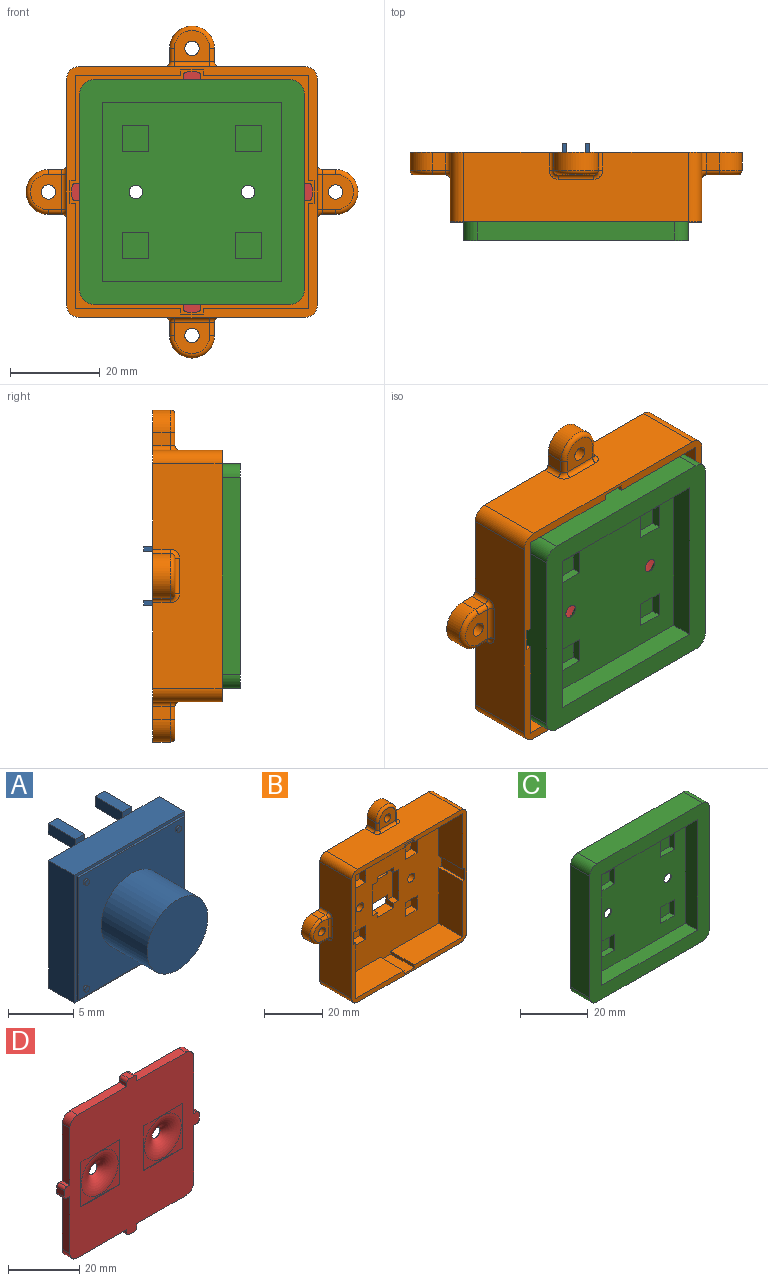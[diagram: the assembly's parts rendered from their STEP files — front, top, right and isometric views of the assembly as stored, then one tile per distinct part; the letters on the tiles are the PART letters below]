
ASSEMBLY  parts=4 mates=3
PART A: 45 faces, bbox 12x11x13 mm
  f0: plane 12x12mm, normal (0,1,0), area 142mm2, adj f17,f18,f19,f20,f22,f23,f24,f27
  f1: plane 11.5x11.5mm, normal (0,-1,0), area 97.3mm2, adj f2,f4,f6,f8,f10,f12,f13,f14
  f2: cylinder r=3.3mm len=6.6mm, axis (0,1,0), area 103.7mm2, adj f1,f3
  f3: plane 6.6x6.6mm, normal (0,-1,0), area 34.2mm2, adj f2
  f4: cylinder r=0.25mm len=0.5mm, axis (0,1,0), area 0.3mm2, adj f1,f5
  f5: plane 0.5x0.5mm, normal (0,-1,0), area 0.2mm2, adj f4
  f6: cylinder r=0.25mm len=0.5mm, axis (0,1,0), area 0.3mm2, adj f1,f7
  f7: plane 0.5x0.5mm, normal (0,-1,0), area 0.2mm2, adj f6
  f8: cylinder r=0.25mm len=0.5mm, axis (0,1,0), area 0.3mm2, adj f1,f9
  f9: plane 0.5x0.5mm, normal (0,-1,0), area 0.2mm2, adj f8
  f10: cylinder r=0.25mm len=0.5mm, axis (0,1,0), area 0.3mm2, adj f1,f11
  f11: plane 0.5x0.5mm, normal (0,-1,0), area 0.2mm2, adj f10
  f12: plane 11.5x0.2mm, normal (-1,0,0), area 2.3mm2, adj f1,f13,f15,f16
  f13: plane 11.5x0.2mm, normal (0,0,1), area 2.3mm2, adj f1,f12,f14,f16
  f14: plane 11.5x0.2mm, normal (1,0,0), area 2.3mm2, adj f1,f13,f15,f16
  f15: plane 11.5x0.2mm, normal (0,0,-1), area 2.3mm2, adj f1,f12,f14,f16
  f16: plane 12x12mm, normal (0,-1,0), area 11.8mm2, adj f12,f13,f14,f15,f17,f18,f19,f20
  f17: plane 12x2.8mm, normal (-1,0,0), area 33.6mm2, adj f0,f16,f18,f20
  f18: plane 12x2.8mm, normal (0,0,1), area 33.6mm2, adj f0,f16,f17,f19,f26,f32
  f19: plane 12x2.8mm, normal (1,0,0), area 33.6mm2, adj f0,f16,f18,f20
  f20: plane 12x2.8mm, normal (0,0,-1), area 33.6mm2, adj f0,f16,f17,f19,f33,f39
  f21: plane 3x1mm, normal (0,0,1), area 3mm2, adj f22,f24,f25,f26
  f22: plane 3x1mm, normal (1,0,0), area 3mm2, adj f0,f21,f23,f25,f26
  f23: plane 3x1mm, normal (0,0,-1), area 3mm2, adj f0,f22,f24,f25
  f24: plane 3x1mm, normal (-1,0,0), area 3mm2, adj f0,f21,f23,f25,f26
  f25: plane 1x1mm, normal (0,1,0), area 1mm2, adj f21,f22,f23,f24
  f26: plane 1x0.5mm, normal (0,-1,0), area 0.5mm2, adj f18,f21,f22,f24
  f27: plane 3x1mm, normal (0,0,-1), area 3mm2, adj f0,f28,f30,f31
  f28: plane 3x1mm, normal (-1,0,0), area 3mm2, adj f0,f27,f29,f31,f32
  f29: plane 3x1mm, normal (0,0,1), area 3mm2, adj f28,f30,f31,f32
  f30: plane 3x1mm, normal (1,0,0), area 3mm2, adj f0,f27,f29,f31,f32
  f31: plane 1x1mm, normal (0,1,0), area 1mm2, adj f27,f28,f29,f30
  f32: plane 1x0.5mm, normal (0,-1,0), area 0.5mm2, adj f18,f28,f29,f30
  f33: plane 1x0.5mm, normal (0,-1,0), area 0.5mm2, adj f20,f34,f35,f36
  f34: plane 3x1mm, normal (1,0,0), area 3mm2, adj f0,f33,f35,f37,f38
  f35: plane 3x1mm, normal (0,0,-1), area 3mm2, adj f33,f34,f36,f38
  f36: plane 3x1mm, normal (-1,0,0), area 3mm2, adj f0,f33,f35,f37,f38
  f37: plane 3x1mm, normal (0,0,1), area 3mm2, adj f0,f34,f36,f38
  f38: plane 1x1mm, normal (0,1,0), area 1mm2, adj f34,f35,f36,f37
  f39: plane 1x0.5mm, normal (0,-1,0), area 0.5mm2, adj f20,f40,f41,f42
  f40: plane 3x1mm, normal (1,0,0), area 3mm2, adj f0,f39,f41,f43,f44
  f41: plane 3x1mm, normal (0,0,-1), area 3mm2, adj f39,f40,f42,f44
  f42: plane 3x1mm, normal (-1,0,0), area 3mm2, adj f0,f39,f41,f43,f44
  f43: plane 3x1mm, normal (0,0,1), area 3mm2, adj f0,f40,f42,f44
  f44: plane 1x1mm, normal (0,1,0), area 1mm2, adj f40,f41,f42,f43
PART B: 120 faces, bbox 74.8x15.5x74.8 mm
  f0: plane 54.4x54.4mm, normal (0,-1,0), area 2374.3mm2, adj f3,f4,f5,f6,f10,f11,f15,f16
  f1: plane 50x15.5mm, normal (1,0,0), area 704.7mm2, adj f7,f12,f45,f46,f84,f86,f88,f90
  f2: plane 50x15.5mm, normal (0,0,1), area 704.7mm2, adj f7,f12,f46,f47,f76,f78,f80,f82
  f3: plane 23.5x11.5mm, normal (1,0,0), area 270.2mm2, adj f0,f7,f31,f34
  f4: plane 23.5x11.5mm, normal (0,0,-1), area 270.2mm2, adj f0,f7,f30,f43
  f5: plane 23.5x11.5mm, normal (-1,0,0), area 270.2mm2, adj f0,f6,f7,f39
  f6: plane 23.5x11.5mm, normal (0,0,1), area 270.2mm2, adj f0,f5,f7,f37
  f7: plane 56x56mm, normal (0,-1,0), area 400.3mm2, adj f1,f2,f3,f4,f5,f6,f13,f14
  f8: plane 8x1mm, normal (0,0,-1), area 8mm2, adj f12,f17,f19,f27
  f9: plane 8x1mm, normal (0,0,1), area 8mm2, adj f10,f11,f12,f27
  f10: plane 4x4mm, normal (-1,0,0), area 10mm2, adj f0,f9,f12,f20,f21,f27
  f11: plane 4x4mm, normal (1,0,0), area 10mm2, adj f0,f9,f12,f20,f22,f27
  f12: plane 74x74mm, normal (0,1,0), area 3332.7mm2, adj f1,f2,f8,f9,f10,f11,f13,f14
  f13: plane 50x15.5mm, normal (-1,0,0), area 704.7mm2, adj f7,f12,f44,f47,f92,f94,f96,f98
  f14: plane 50x15.5mm, normal (0,0,-1), area 704.7mm2, adj f7,f12,f44,f45,f68,f70,f72,f74
  f15: cylinder r=1.7mm len=4mm, axis (0,1,0), area 42.7mm2, adj f0,f12
  f16: cylinder r=1.7mm len=4mm, axis (0,1,0), area 42.7mm2, adj f0,f12
  f17: plane 4x4mm, normal (1,0,0), area 10mm2, adj f0,f8,f12,f18,f24,f27
  f18: plane 8x4mm, normal (0,0,1), area 32mm2, adj f0,f12,f17,f19
  f19: plane 4x4mm, normal (-1,0,0), area 10mm2, adj f0,f8,f12,f18,f25,f27
  f20: plane 8x4mm, normal (0,0,-1), area 32mm2, adj f0,f10,f11,f12
  f21: plane 3x2.5mm, normal (0,0,-1), area 7.5mm2, adj f0,f10,f26,f27
  f22: plane 3x2.5mm, normal (0,0,-1), area 7.5mm2, adj f0,f11,f23,f27
  f23: plane 13x3mm, normal (1,0,0), area 39mm2, adj f0,f22,f24,f27
  f24: plane 3x2.5mm, normal (0,0,1), area 7.5mm2, adj f0,f17,f23,f27
  f25: plane 3x2.5mm, normal (0,0,1), area 7.5mm2, adj f0,f19,f26,f27
  f26: plane 13x3mm, normal (-1,0,0), area 39mm2, adj f0,f21,f25,f27
  f27: plane 13x13mm, normal (0,-1,0), area 137mm2, adj f8,f9,f10,f11,f17,f19,f21,f22
  f28: plane 23.5x11.5mm, normal (1,0,0), area 270.2mm2, adj f0,f7,f29,f32
  f29: plane 23.5x11.5mm, normal (0,0,-1), area 270.2mm2, adj f0,f7,f28,f42
  f30: plane 23.5x11.5mm, normal (-1,0,0), area 270.2mm2, adj f0,f4,f7,f38
  f31: plane 23.5x11.5mm, normal (0,0,1), area 270.2mm2, adj f0,f3,f7,f35
  f32: plane 11.5x1.2mm, normal (0,0,-1), area 13.8mm2, adj f0,f7,f28,f33
  f33: plane 11.5x5mm, normal (1,0,0), area 57.5mm2, adj f0,f7,f32,f34
  f34: plane 11.5x1.2mm, normal (0,0,1), area 13.8mm2, adj f0,f3,f7,f33
  f35: plane 11.5x1.2mm, normal (1,0,0), area 13.8mm2, adj f0,f7,f31,f36
  f36: plane 11.5x5mm, normal (0,0,1), area 57.5mm2, adj f0,f7,f35,f37
  f37: plane 11.5x1.2mm, normal (-1,0,0), area 13.8mm2, adj f0,f6,f7,f36
  f38: plane 11.5x1.2mm, normal (0,0,-1), area 13.8mm2, adj f0,f7,f30,f40
  f39: plane 11.5x1.2mm, normal (0,0,1), area 13.8mm2, adj f0,f5,f7,f40
  f40: plane 11.5x5mm, normal (-1,0,0), area 57.5mm2, adj f0,f7,f38,f39
  f41: plane 11.5x5mm, normal (0,0,-1), area 57.5mm2, adj f0,f7,f42,f43
  f42: plane 11.5x1.2mm, normal (1,0,0), area 13.8mm2, adj f0,f7,f29,f41
  f43: plane 11.5x1.2mm, normal (-1,0,0), area 13.8mm2, adj f0,f4,f7,f41
  f44: cylinder r=3mm len=15.5mm, axis (0,1,0), area 73mm2, adj f7,f12,f13,f14
  f45: cylinder r=3mm len=15.5mm, axis (0,-1,0), area 73mm2, adj f1,f7,f12,f14
  f46: cylinder r=3mm len=15.5mm, axis (0,1,0), area 73mm2, adj f1,f2,f7,f12
  f47: cylinder r=3mm len=15.5mm, axis (0,-1,0), area 73mm2, adj f2,f7,f12,f13
  f48: cylinder r=5mm len=10mm, axis (0,1,0), area 62.8mm2, adj f12,f49,f51,f79
  f49: plane 4x3mm, normal (-1,0,0), area 12mm2, adj f12,f48,f76,f77
  f50: cylinder r=1.6mm len=5mm, axis (0,1,0), area 50.3mm2, adj f12,f52
  f51: plane 4x3mm, normal (1,0,0), area 12mm2, adj f12,f48,f81,f83
  f52: plane 8x7mm, normal (0,-1,0), area 41.1mm2, adj f50,f77,f79,f80,f81
  f53: plane 4x3mm, normal (-1,0,0), area 12mm2, adj f12,f54,f73,f75
  f54: cylinder r=5mm len=10mm, axis (0,1,0), area 62.8mm2, adj f12,f53,f55,f71
  f55: plane 4x3mm, normal (1,0,0), area 12mm2, adj f12,f54,f68,f69
  f56: cylinder r=1.6mm len=5mm, axis (0,1,0), area 50.3mm2, adj f12,f57
  f57: plane 8x7mm, normal (0,-1,0), area 41.1mm2, adj f56,f69,f71,f72,f73
  f58: plane 4x3mm, normal (0,0,1), area 12mm2, adj f12,f59,f97,f99
  f59: cylinder r=5mm len=10mm, axis (0,1,0), area 62.8mm2, adj f12,f58,f60,f95
  f60: plane 4x3mm, normal (0,0,-1), area 12mm2, adj f12,f59,f92,f93
  f61: cylinder r=1.6mm len=5mm, axis (0,1,0), area 50.3mm2, adj f12,f62
  f62: plane 8x7mm, normal (0,-1,0), area 41.1mm2, adj f61,f93,f95,f96,f97
  f63: cylinder r=5mm len=10mm, axis (0,1,0), area 62.8mm2, adj f12,f64,f66,f87
  f64: plane 4x3mm, normal (0,0,1), area 12mm2, adj f12,f63,f84,f85
  f65: cylinder r=1.6mm len=5mm, axis (0,1,0), area 50.3mm2, adj f12,f67
  f66: plane 4x3mm, normal (0,0,-1), area 12mm2, adj f12,f63,f89,f91
  f67: plane 8x7mm, normal (0,-1,0), area 41.1mm2, adj f65,f85,f87,f88,f89
  f68: cylinder r=1mm len=4mm, axis (0,-1,0), area 6.3mm2, adj f12,f14,f55,f70
  f69: cylinder r=1mm len=3mm, axis (0,0,-1), area 4.7mm2, adj f55,f57,f70,f71
  f70: torus R=2mm, axis (0,0,1), area 3.4mm2, adj f14,f68,f69,f72
  f71: torus R=4mm, axis (0,-1,0), area 22.9mm2, adj f54,f57,f69,f73
  f72: cylinder r=1mm len=8mm, axis (1,0,0), area 12.6mm2, adj f14,f57,f70,f74
  f73: cylinder r=1mm len=3mm, axis (0,0,1), area 4.7mm2, adj f53,f57,f71,f74
  f74: torus R=2mm, axis (0,0,1), area 3.4mm2, adj f14,f72,f73,f75
  f75: cylinder r=1mm len=4mm, axis (0,1,0), area 6.3mm2, adj f12,f14,f53,f74
  f76: cylinder r=1mm len=4mm, axis (0,1,0), area 6.3mm2, adj f2,f12,f49,f78
  f77: cylinder r=1mm len=3mm, axis (0,0,1), area 4.7mm2, adj f49,f52,f78,f79
  f78: torus R=2mm, axis (0,0,1), area 3.4mm2, adj f2,f76,f77,f80
  f79: torus R=4mm, axis (0,-1,0), area 22.9mm2, adj f48,f52,f77,f81
  f80: cylinder r=1mm len=8mm, axis (-1,0,0), area 12.6mm2, adj f2,f52,f78,f82
  f81: cylinder r=1mm len=3mm, axis (0,0,-1), area 4.7mm2, adj f51,f52,f79,f82
  f82: torus R=2mm, axis (0,0,1), area 3.4mm2, adj f2,f80,f81,f83
  f83: cylinder r=1mm len=4mm, axis (0,-1,0), area 6.3mm2, adj f2,f12,f51,f82
  f84: cylinder r=1mm len=4mm, axis (0,1,0), area 6.3mm2, adj f1,f12,f64,f86
  f85: cylinder r=1mm len=3mm, axis (1,0,0), area 4.7mm2, adj f64,f67,f86,f87
  f86: torus R=2mm, axis (1,0,0), area 3.4mm2, adj f1,f84,f85,f88
  f87: torus R=4mm, axis (0,-1,0), area 22.9mm2, adj f63,f67,f85,f89
  f88: cylinder r=1mm len=8mm, axis (0,0,1), area 12.6mm2, adj f1,f67,f86,f90
  f89: cylinder r=1mm len=3mm, axis (-1,0,0), area 4.7mm2, adj f66,f67,f87,f90
  f90: torus R=2mm, axis (1,0,0), area 3.4mm2, adj f1,f88,f89,f91
  f91: cylinder r=1mm len=4mm, axis (0,-1,0), area 6.3mm2, adj f1,f12,f66,f90
  f92: cylinder r=1mm len=4mm, axis (0,-1,0), area 6.3mm2, adj f12,f13,f60,f94
  f93: cylinder r=1mm len=3mm, axis (-1,0,0), area 4.7mm2, adj f60,f62,f94,f95
  f94: torus R=2mm, axis (1,0,0), area 3.4mm2, adj f13,f92,f93,f96
  f95: torus R=4mm, axis (0,-1,0), area 22.9mm2, adj f59,f62,f93,f97
  f96: cylinder r=1mm len=8mm, axis (0,0,-1), area 12.6mm2, adj f13,f62,f94,f98
  f97: cylinder r=1mm len=3mm, axis (1,0,0), area 4.7mm2, adj f58,f62,f95,f98
  f98: torus R=2mm, axis (1,0,0), area 3.4mm2, adj f13,f96,f97,f99
  f99: cylinder r=1mm len=4mm, axis (0,1,0), area 6.3mm2, adj f12,f13,f58,f98
  f100: plane 5.8x3mm, normal (0,0,1), area 17.4mm2, adj f0,f101,f103,f104
  f101: plane 5.8x3mm, normal (-1,0,0), area 17.4mm2, adj f0,f100,f102,f104
  f102: plane 5.8x3mm, normal (0,0,-1), area 17.4mm2, adj f0,f101,f103,f104
  f103: plane 5.8x3mm, normal (1,0,0), area 17.4mm2, adj f0,f100,f102,f104
  f104: plane 5.8x5.8mm, normal (0,-1,0), area 33.6mm2, adj f100,f101,f102,f103
  f105: plane 5.8x3mm, normal (0,0,1), area 17.4mm2, adj f0,f106,f108,f109
  f106: plane 5.8x3mm, normal (-1,0,0), area 17.4mm2, adj f0,f105,f107,f109
  f107: plane 5.8x3mm, normal (0,0,-1), area 17.4mm2, adj f0,f106,f108,f109
  f108: plane 5.8x3mm, normal (1,0,0), area 17.4mm2, adj f0,f105,f107,f109
  f109: plane 5.8x5.8mm, normal (0,-1,0), area 33.6mm2, adj f105,f106,f107,f108
  f110: plane 5.8x3mm, normal (0,0,1), area 17.4mm2, adj f0,f111,f113,f114
  f111: plane 5.8x3mm, normal (-1,0,0), area 17.4mm2, adj f0,f110,f112,f114
  f112: plane 5.8x3mm, normal (0,0,-1), area 17.4mm2, adj f0,f111,f113,f114
  f113: plane 5.8x3mm, normal (1,0,0), area 17.4mm2, adj f0,f110,f112,f114
  f114: plane 5.8x5.8mm, normal (0,-1,0), area 33.6mm2, adj f110,f111,f112,f113
  f115: plane 5.8x3mm, normal (0,0,1), area 17.4mm2, adj f0,f116,f118,f119
  f116: plane 5.8x3mm, normal (-1,0,0), area 17.4mm2, adj f0,f115,f117,f119
  f117: plane 5.8x3mm, normal (0,0,-1), area 17.4mm2, adj f0,f116,f118,f119
  f118: plane 5.8x3mm, normal (1,0,0), area 17.4mm2, adj f0,f115,f117,f119
  f119: plane 5.8x5.8mm, normal (0,-1,0), area 33.6mm2, adj f115,f116,f117,f118
PART C: 47 faces, bbox 50x15.1x50 mm
  f0: plane 40x40mm, normal (0,-1,0), area 1451.3mm2, adj f6,f7,f8,f9,f25,f26,f27,f28
  f1: plane 50x50mm, normal (0,1,0), area 2018mm2, adj f2,f3,f4,f5,f11,f12,f13,f14
  f2: plane 44x8mm, normal (0,0,1), area 352mm2, adj f1,f10,f21,f24
  f3: plane 44x8mm, normal (-1,0,0), area 352mm2, adj f1,f10,f21,f22
  f4: plane 44x8mm, normal (0,0,-1), area 352mm2, adj f1,f10,f22,f23
  f5: plane 44x8mm, normal (1,0,0), area 352mm2, adj f1,f10,f23,f24
  f6: plane 40x5mm, normal (1,0,0), area 200mm2, adj f0,f7,f9,f10
  f7: plane 40x5mm, normal (0,0,-1), area 200mm2, adj f0,f6,f8,f10
  f8: plane 40x5mm, normal (-1,0,0), area 200mm2, adj f0,f7,f9,f10
  f9: plane 40x5mm, normal (0,0,1), area 200mm2, adj f0,f6,f8,f10
  f10: plane 50x50mm, normal (0,-1,0), area 892.3mm2, adj f2,f3,f4,f5,f6,f7,f8,f9
  f11: plane 15.4x0.2mm, normal (0,0,-1), area 3.1mm2, adj f1,f12,f14,f15
  f12: plane 15.4x0.2mm, normal (-1,0,0), area 3.1mm2, adj f1,f11,f13,f15
  f13: plane 15.4x0.2mm, normal (0,0,1), area 3.1mm2, adj f1,f12,f14,f15
  f14: plane 15.4x0.2mm, normal (1,0,0), area 3.1mm2, adj f1,f11,f13,f15
  f15: plane 15.4x15.4mm, normal (0,1,0), area 67.7mm2, adj f11,f12,f13,f14,f45
  f16: plane 15.4x0.2mm, normal (0,0,-1), area 3.1mm2, adj f1,f17,f19,f20
  f17: plane 15.4x0.2mm, normal (-1,0,0), area 3.1mm2, adj f1,f16,f18,f20
  f18: plane 15.4x0.2mm, normal (0,0,1), area 3.1mm2, adj f1,f17,f19,f20
  f19: plane 15.4x0.2mm, normal (1,0,0), area 3.1mm2, adj f1,f16,f18,f20
  f20: plane 15.4x15.4mm, normal (0,1,0), area 67.7mm2, adj f16,f17,f18,f19,f46
  f21: cylinder r=3mm len=8mm, axis (0,-1,0), area 37.7mm2, adj f1,f2,f3,f10
  f22: cylinder r=3mm len=8mm, axis (0,1,0), area 37.7mm2, adj f1,f3,f4,f10
  f23: cylinder r=3mm len=8mm, axis (0,-1,0), area 37.7mm2, adj f1,f4,f5,f10
  f24: cylinder r=3mm len=8mm, axis (0,1,0), area 37.7mm2, adj f1,f2,f5,f10
  f25: plane 5.8x2mm, normal (0,0,1), area 11.6mm2, adj f0,f26,f28,f29
  f26: plane 5.8x2mm, normal (-1,0,0), area 11.6mm2, adj f0,f25,f27,f29
  f27: plane 5.8x2mm, normal (0,0,-1), area 11.6mm2, adj f0,f26,f28,f29
  f28: plane 5.8x2mm, normal (1,0,0), area 11.6mm2, adj f0,f25,f27,f29
  f29: plane 5.8x5.8mm, normal (0,-1,0), area 33.6mm2, adj f25,f26,f27,f28
  f30: plane 5.8x2mm, normal (0,0,1), area 11.6mm2, adj f0,f31,f33,f34
  f31: plane 5.8x2mm, normal (-1,0,0), area 11.6mm2, adj f0,f30,f32,f34
  f32: plane 5.8x2mm, normal (0,0,-1), area 11.6mm2, adj f0,f31,f33,f34
  f33: plane 5.8x2mm, normal (1,0,0), area 11.6mm2, adj f0,f30,f32,f34
  f34: plane 5.8x5.8mm, normal (0,-1,0), area 33.6mm2, adj f30,f31,f32,f33
  f35: plane 5.8x2mm, normal (0,0,1), area 11.6mm2, adj f0,f36,f38,f39
  f36: plane 5.8x2mm, normal (-1,0,0), area 11.6mm2, adj f0,f35,f37,f39
  f37: plane 5.8x2mm, normal (0,0,-1), area 11.6mm2, adj f0,f36,f38,f39
  f38: plane 5.8x2mm, normal (1,0,0), area 11.6mm2, adj f0,f35,f37,f39
  f39: plane 5.8x5.8mm, normal (0,-1,0), area 33.6mm2, adj f35,f36,f37,f38
  f40: plane 5.8x2mm, normal (0,0,1), area 11.6mm2, adj f0,f41,f43,f44
  f41: plane 5.8x2mm, normal (-1,0,0), area 11.6mm2, adj f0,f40,f42,f44
  f42: plane 5.8x2mm, normal (0,0,-1), area 11.6mm2, adj f0,f41,f43,f44
  f43: plane 5.8x2mm, normal (1,0,0), area 11.6mm2, adj f0,f40,f42,f44
  f44: plane 5.8x5.8mm, normal (0,-1,0), area 33.6mm2, adj f40,f41,f42,f43
  f45: torus R=7.34mm, axis (0,1,0), area 177.3mm2, adj f0,f15
  f46: torus R=7.34mm, axis (0,1,0), area 177.3mm2, adj f0,f20
PART D: 66 faces, bbox 53.5x7.2x53.5 mm
  f0: plane 53.5x53.5mm, normal (0,-1,0), area 1962.2mm2, adj f2,f3,f4,f5,f6,f7,f8,f9
  f1: plane 53.5x53.5mm, normal (0,1,0), area 2283.8mm2, adj f2,f3,f4,f5,f6,f7,f8,f9
  f2: plane 3x1.2mm, normal (-1,0,0), area 3.6mm2, adj f0,f1,f3,f59
  f3: plane 19.55x3mm, normal (0,0,1), area 58.6mm2, adj f0,f1,f2,f24
  f4: plane 19.55x3mm, normal (-1,0,0), area 58.6mm2, adj f0,f1,f5,f24
  f5: plane 3x1.2mm, normal (0,0,1), area 3.6mm2, adj f0,f1,f4,f60
  f6: plane 3x2mm, normal (-1,0,0), area 6mm2, adj f0,f1,f60,f61
  f7: plane 3x1.2mm, normal (0,0,-1), area 3.6mm2, adj f0,f1,f8,f61
  f8: plane 19.55x3mm, normal (-1,0,0), area 58.6mm2, adj f0,f1,f7,f25
  f9: plane 19.55x3mm, normal (0,0,-1), area 58.6mm2, adj f0,f1,f10,f25
  f10: plane 3x1.2mm, normal (-1,0,0), area 3.6mm2, adj f0,f1,f9,f62
  f11: plane 3x2mm, normal (0,0,-1), area 6mm2, adj f0,f1,f62,f63
  f12: plane 3x1.2mm, normal (1,0,0), area 3.6mm2, adj f0,f1,f13,f63
  f13: plane 19.55x3mm, normal (0,0,-1), area 58.6mm2, adj f0,f1,f12,f22
  f14: plane 19.55x3mm, normal (1,0,0), area 58.6mm2, adj f0,f1,f15,f22
  f15: plane 3x1.2mm, normal (0,0,-1), area 3.6mm2, adj f0,f1,f14,f64
  f16: plane 3x2mm, normal (1,0,0), area 6mm2, adj f0,f1,f64,f65
  f17: plane 3x1.2mm, normal (0,0,1), area 3.6mm2, adj f0,f1,f18,f65
  f18: plane 19.55x3mm, normal (1,0,0), area 58.6mm2, adj f0,f1,f17,f23
  f19: plane 19.55x3mm, normal (0,0,1), area 58.6mm2, adj f0,f1,f20,f23
  f20: plane 3x1.2mm, normal (1,0,0), area 3.6mm2, adj f0,f1,f19,f58
  f21: plane 3x2mm, normal (0,0,1), area 6mm2, adj f0,f1,f58,f59
  f22: cylinder r=3mm len=3mm, axis (0,-1,0), area 14.1mm2, adj f0,f1,f13,f14
  f23: cylinder r=3mm len=3mm, axis (0,1,0), area 14.1mm2, adj f0,f1,f18,f19
  f24: cylinder r=3mm len=3mm, axis (0,-1,0), area 14.1mm2, adj f0,f1,f3,f4
  f25: cylinder r=3mm len=3mm, axis (0,1,0), area 14.1mm2, adj f0,f1,f8,f9
  f26: plane 5.8x2mm, normal (0,0,1), area 11.6mm2, adj f1,f27,f29,f30
  f27: plane 5.8x2mm, normal (1,0,0), area 11.6mm2, adj f1,f26,f28,f30
  f28: plane 5.8x2mm, normal (0,0,-1), area 11.6mm2, adj f1,f27,f29,f30
  f29: plane 5.8x2mm, normal (-1,0,0), area 11.6mm2, adj f1,f26,f28,f30
  f30: plane 5.8x5.8mm, normal (0,1,0), area 33.6mm2, adj f26,f27,f28,f29
  f31: plane 5.8x2mm, normal (0,0,1), area 11.6mm2, adj f1,f32,f34,f35
  f32: plane 5.8x2mm, normal (1,0,0), area 11.6mm2, adj f1,f31,f33,f35
  f33: plane 5.8x2mm, normal (0,0,-1), area 11.6mm2, adj f1,f32,f34,f35
  f34: plane 5.8x2mm, normal (-1,0,0), area 11.6mm2, adj f1,f31,f33,f35
  f35: plane 5.8x5.8mm, normal (0,1,0), area 33.6mm2, adj f31,f32,f33,f34
  f36: plane 5.8x2mm, normal (0,0,1), area 11.6mm2, adj f1,f37,f39,f40
  f37: plane 5.8x2mm, normal (1,0,0), area 11.6mm2, adj f1,f36,f38,f40
  f38: plane 5.8x2mm, normal (0,0,-1), area 11.6mm2, adj f1,f37,f39,f40
  f39: plane 5.8x2mm, normal (-1,0,0), area 11.6mm2, adj f1,f36,f38,f40
  f40: plane 5.8x5.8mm, normal (0,1,0), area 33.6mm2, adj f36,f37,f38,f39
  f41: plane 5.8x2mm, normal (0,0,1), area 11.6mm2, adj f1,f42,f44,f45
  f42: plane 5.8x2mm, normal (1,0,0), area 11.6mm2, adj f1,f41,f43,f45
  f43: plane 5.8x2mm, normal (0,0,-1), area 11.6mm2, adj f1,f42,f44,f45
  f44: plane 5.8x2mm, normal (-1,0,0), area 11.6mm2, adj f1,f41,f43,f45
  f45: plane 5.8x5.8mm, normal (0,1,0), area 33.6mm2, adj f41,f42,f43,f44
  f46: plane 15.4x0.2mm, normal (0,0,-1), area 3.1mm2, adj f0,f47,f49,f50
  f47: plane 15.4x0.2mm, normal (1,0,0), area 3.1mm2, adj f0,f46,f48,f50
  f48: plane 15.4x0.2mm, normal (0,0,1), area 3.1mm2, adj f0,f47,f49,f50
  f49: plane 15.4x0.2mm, normal (-1,0,0), area 3.1mm2, adj f0,f46,f48,f50
  f50: plane 15.4x15.4mm, normal (0,-1,0), area 69.7mm2, adj f46,f47,f48,f49,f57
  f51: plane 15.4x0.2mm, normal (0,0,-1), area 3.1mm2, adj f0,f52,f54,f55
  f52: plane 15.4x0.2mm, normal (1,0,0), area 3.1mm2, adj f0,f51,f53,f55
  f53: plane 15.4x0.2mm, normal (0,0,1), area 3.1mm2, adj f0,f52,f54,f55
  f54: plane 15.4x0.2mm, normal (-1,0,0), area 3.1mm2, adj f0,f51,f53,f55
  f55: plane 15.4x15.4mm, normal (0,-1,0), area 69.7mm2, adj f51,f52,f53,f54,f56
  f56: torus R=7.3mm, axis (0,-1,0), area 174.6mm2, adj f1,f55
  f57: torus R=7.3mm, axis (0,-1,0), area 174.6mm2, adj f1,f50
  f58: cylinder r=1mm len=3mm, axis (0,-1,0), area 4.7mm2, adj f0,f1,f20,f21
  f59: cylinder r=1mm len=3mm, axis (0,1,0), area 4.7mm2, adj f0,f1,f2,f21
  f60: cylinder r=1mm len=3mm, axis (0,-1,0), area 4.7mm2, adj f0,f1,f5,f6
  f61: cylinder r=1mm len=3mm, axis (0,1,0), area 4.7mm2, adj f0,f1,f6,f7
  f62: cylinder r=1mm len=3mm, axis (0,1,0), area 4.7mm2, adj f0,f1,f10,f11
  f63: cylinder r=1mm len=3mm, axis (0,-1,0), area 4.7mm2, adj f0,f1,f11,f12
  f64: cylinder r=1mm len=3mm, axis (0,-1,0), area 4.7mm2, adj f0,f1,f15,f16
  f65: cylinder r=1mm len=3mm, axis (0,1,0), area 4.7mm2, adj f0,f1,f16,f17
PLACE A t=(-29.8,3,26.99)mm
PLACE B t=(15.88,4,39.56)mm fixed
PLACE C t=(-25.15,-7.6,24.26)mm
PLACE D t=(-18.68,-5,39.56)mm
MATE fastened D.f56 <-> C.f46  axis (0,-1,0) through (-6.18,-7.8,39.56)mm
MATE fastened A.f2 <-> B.f27  axis (0,1,0) through (-18.68,3,39.56)mm
MATE fastened D.f1 <-> A.f2  axis (0,1,0) through (-18.68,-5,39.56)mm
